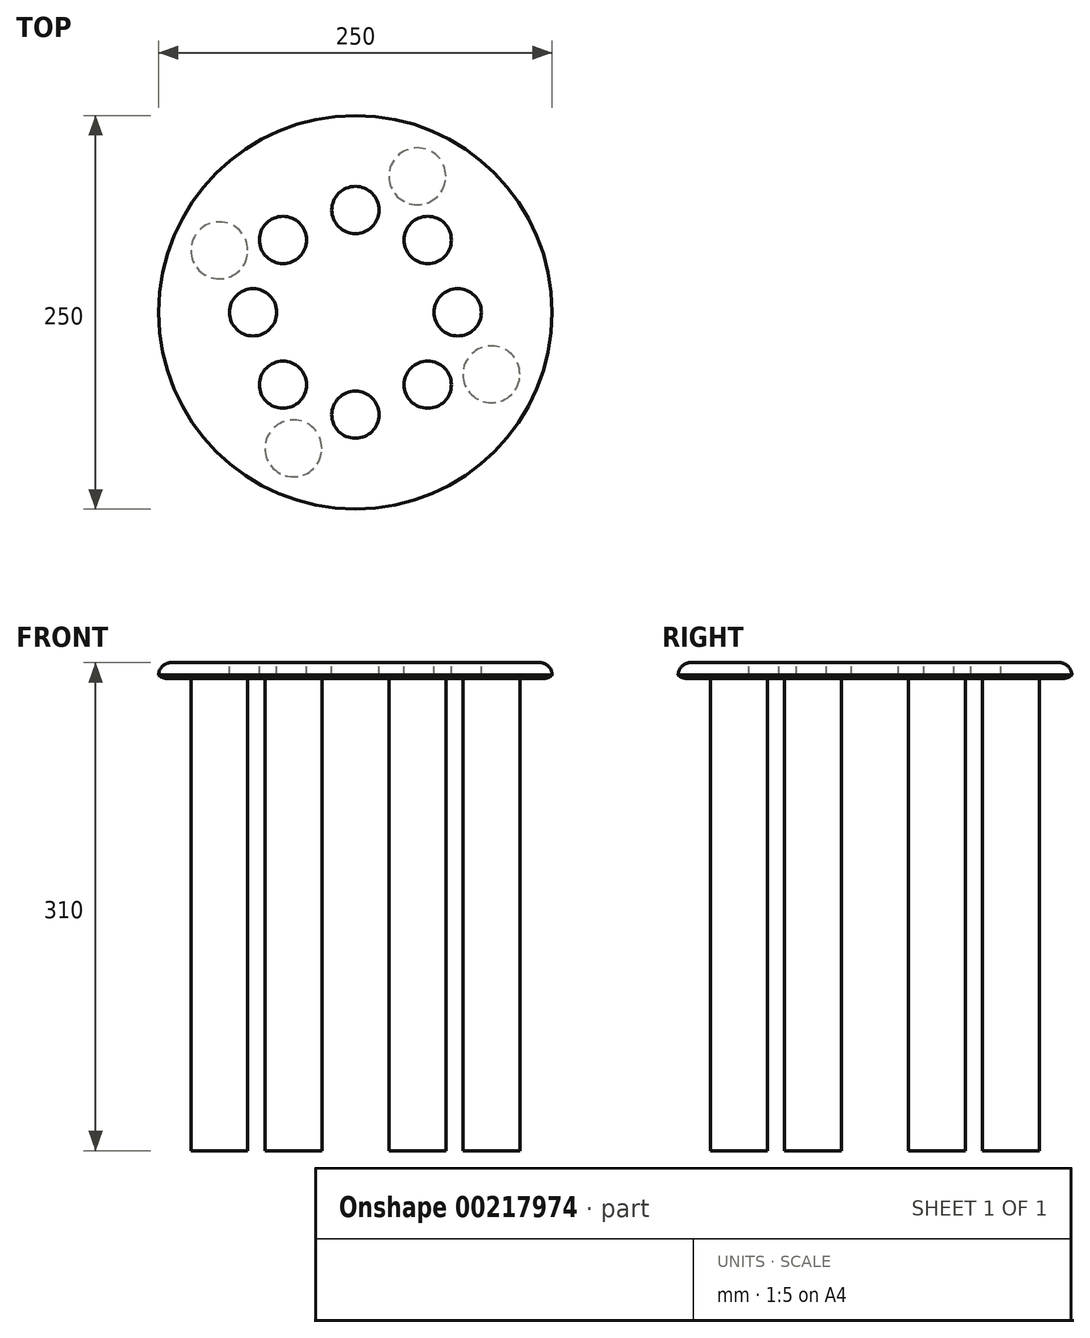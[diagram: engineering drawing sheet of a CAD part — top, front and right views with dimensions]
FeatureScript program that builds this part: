
annotation { "Feature Type Name" : "Feature", "Feature Type Description" : "" }
export const myFeature = defineFeature(function(context is Context, id is Id, definition is map)
    precondition{}
    {
        {
            var Q0;
            Q0=qCreatedBy(makeId("Top.planeOp"),FACE);
            var sketch = newSketch(context, id + "F0", { "sketchPlane" : qUnion([Q0])});
            skCircle(sketch, "E0", {"center": v(0, 0) * mm, "radius": 125 * mm});
            skSolve(sketch);
        }
        {
            var Q0;
            Q0=makeQuery(id+"F0.imprint","IMPRINT",FACE,{"disambiguationData":[TD([[makeQuery(id+"F0.imprint","IMPRINT",EDGE,{"derivedFrom":sQuery(id+"F0.wireOp",EDGE,"E0")}),1.0]])]});
            var sketch = newSketch(context, id + "F1", { "sketchPlane" : qUnion([Q0])});
            skCircle(sketch, "E1", {"center": v(0, 65) * mm, "radius": 15 * mm});
            skCircle(sketch, "E2.1.0", {"center": v(-45.96, 45.96) * mm, "radius": 15 * mm});
            skCircle(sketch, "E2.2.0", {"center": v(-65, 0) * mm, "radius": 15 * mm});
            skCircle(sketch, "E2.3.0", {"center": v(-45.96, -45.96) * mm, "radius": 15 * mm});
            skCircle(sketch, "E2.4.0", {"center": v(0, -65) * mm, "radius": 15 * mm});
            skCircle(sketch, "E2.5.0", {"center": v(45.96, -45.96) * mm, "radius": 15 * mm});
            skCircle(sketch, "E2.6.0", {"center": v(65, 0) * mm, "radius": 15 * mm});
            skCircle(sketch, "E2.7.0", {"center": v(45.96, 45.96) * mm, "radius": 15 * mm});
            skPoint(sketch, "E2.center", {"position": v(0, 0) * mm});
            skSolve(sketch);
        }
        {
            var Q0;
            Q0=makeQuery(id+"F0.imprint","IMPRINT",FACE,{"disambiguationData":[TD([[makeQuery(id+"F0.imprint","IMPRINT",EDGE,{"derivedFrom":sQuery(id+"F0.wireOp",EDGE,"E0")}),1.0]])]});
            extrude(context, id + "F2", {"entities" : qUnion([Q0]), "depth" : 10 * mm});
        }
        {
            var Q0;
            Q0=makeQuery(id+"F1.imprint","IMPRINT",FACE,{"disambiguationData":[TD([[makeQuery(id+"F1.imprint","IMPRINT",EDGE,{"derivedFrom":sQuery(id+"F1.wireOp",EDGE,"E2.3.0")}),1.0]])]});
            var Q1;
            Q1=makeQuery(id+"F1.imprint","IMPRINT",FACE,{"disambiguationData":[TD([[makeQuery(id+"F1.imprint","IMPRINT",EDGE,{"derivedFrom":sQuery(id+"F1.wireOp",EDGE,"E2.2.0")}),1.0]])]});
            var Q2;
            Q2=makeQuery(id+"F1.imprint","IMPRINT",FACE,{"disambiguationData":[TD([[makeQuery(id+"F1.imprint","IMPRINT",EDGE,{"derivedFrom":sQuery(id+"F1.wireOp",EDGE,"E1")}),1.0]])]});
            var Q3;
            Q3=makeQuery(id+"F1.imprint","IMPRINT",FACE,{"disambiguationData":[TD([[makeQuery(id+"F1.imprint","IMPRINT",EDGE,{"derivedFrom":sQuery(id+"F1.wireOp",EDGE,"E2.4.0")}),1.0]])]});
            var Q4;
            Q4=makeQuery(id+"F1.imprint","IMPRINT",FACE,{"disambiguationData":[TD([[makeQuery(id+"F1.imprint","IMPRINT",EDGE,{"derivedFrom":sQuery(id+"F1.wireOp",EDGE,"E2.5.0")}),1.0]])]});
            var Q5;
            Q5=makeQuery(id+"F1.imprint","IMPRINT",FACE,{"disambiguationData":[TD([[makeQuery(id+"F1.imprint","IMPRINT",EDGE,{"derivedFrom":sQuery(id+"F1.wireOp",EDGE,"E2.6.0")}),1.0]])]});
            var Q6;
            Q6=makeQuery(id+"F1.imprint","IMPRINT",FACE,{"disambiguationData":[TD([[makeQuery(id+"F1.imprint","IMPRINT",EDGE,{"derivedFrom":sQuery(id+"F1.wireOp",EDGE,"E2.7.0")}),1.0]])]});
            var Q7;
            Q7=makeQuery(id+"F1.imprint","IMPRINT",FACE,{"disambiguationData":[TD([[makeQuery(id+"F1.imprint","IMPRINT",EDGE,{"derivedFrom":sQuery(id+"F1.wireOp",EDGE,"E2.1.0")}),1.0]])]});
            extrude(context, id + "F3", {"entities" : qUnion([Q0, Q1, Q2, Q3, Q4, Q5, Q6, Q7]), "operationType" : NewBodyOperationType.ADD, "depth" : 39 * mm});
        }
        {
            var Q0;
            Q0=makeQuery(id+"F3.opExtrude","CAP_FACE",FACE,{"disambiguationData":[OSD([sQuery(id+"F1.wireOp",EDGE,"E2.3.0")])],"isStart":false});
            var Q1;
            Q1=makeQuery(id+"F3.opExtrude","CAP_FACE",FACE,{"disambiguationData":[OSD([sQuery(id+"F1.wireOp",EDGE,"E2.4.0")])],"isStart":false});
            var Q2;
            Q2=makeQuery(id+"F3.opExtrude","CAP_FACE",FACE,{"disambiguationData":[OSD([sQuery(id+"F1.wireOp",EDGE,"E2.5.0")])],"isStart":false});
            var Q3;
            Q3=makeQuery(id+"F3.opExtrude","CAP_FACE",FACE,{"disambiguationData":[OSD([sQuery(id+"F1.wireOp",EDGE,"E2.6.0")])],"isStart":false});
            var Q4;
            Q4=makeQuery(id+"F3.opExtrude","CAP_FACE",FACE,{"disambiguationData":[OSD([sQuery(id+"F1.wireOp",EDGE,"E2.7.0")])],"isStart":false});
            var Q5;
            Q5=makeQuery(id+"F3.opExtrude","CAP_FACE",FACE,{"disambiguationData":[OSD([sQuery(id+"F1.wireOp",EDGE,"E1")])],"isStart":false});
            var Q6;
            Q6=makeQuery(id+"F3.opExtrude","CAP_FACE",FACE,{"disambiguationData":[OSD([sQuery(id+"F1.wireOp",EDGE,"E2.1.0")])],"isStart":false});
            var Q7;
            Q7=makeQuery(id+"F3.opExtrude","CAP_FACE",FACE,{"disambiguationData":[OSD([sQuery(id+"F1.wireOp",EDGE,"E2.2.0")])],"isStart":false});
            extrude(context, id + "F4", {"entities" : qUnion([Q0, Q1, Q2, Q3, Q4, Q5, Q6, Q7]), "operationType" : NewBodyOperationType.REMOVE, "oppositeDirection" : true, "depth" : 107 * mm});
        }
        {
            var Q0;
            Q0=makeQuery(id+"F2.opExtrude","CAP_EDGE",EDGE,{"disambiguationData":[OSD([sQuery(id+"F0.wireOp",EDGE,"E0")])],"isStart":false});
            fillet(context, id + "F5", {"entities" : qUnion([Q0]), "radius" : 8 * mm, "tangentPropagation" : true, "allowEdgeOverflow" : false});
        }
        {
            var Q0;
            Q0=makeQuery(id+"F2.opExtrude","CAP_EDGE",EDGE,{"disambiguationData":[OSD([sQuery(id+"F0.wireOp",EDGE,"E0")])],"isStart":true});
            fillet(context, id + "F6", {"entities" : qUnion([Q0]), "radius" : 8 * mm, "tangentPropagation" : true, "allowEdgeOverflow" : false});
        }
        {
            var Q0;
            Q0=makeQuery(id+"F2.opExtrude","CAP_FACE",FACE,{"disambiguationData":[OSD([sQuery(id+"F0.wireOp",EDGE,"E0")])],"isStart":true});
            var sketch = newSketch(context, id + "F7", { "sketchPlane" : qUnion([Q0])});
            skCircle(sketch, "E3", {"center": v(39.36, -86.4) * mm, "radius": 18.07 * mm});
            skCircle(sketch, "E4.1.0", {"center": v(86.4, 39.36) * mm, "radius": 18.07 * mm});
            skCircle(sketch, "E4.2.0", {"center": v(-39.36, 86.4) * mm, "radius": 18.07 * mm});
            skCircle(sketch, "E4.3.0", {"center": v(-86.4, -39.36) * mm, "radius": 18.07 * mm});
            skPoint(sketch, "E4.center", {"position": v(0, 0) * mm});
            skSolve(sketch);
        }
        {
            var Q0;
            Q0=makeQuery(id+"F7.imprint","IMPRINT",FACE,{"disambiguationData":[TD([[makeQuery(id+"F7.imprint","IMPRINT",EDGE,{"derivedFrom":sQuery(id+"F7.wireOp",EDGE,"E3")}),1.0]])]});
            var Q1;
            Q1=makeQuery(id+"F7.imprint","IMPRINT",FACE,{"disambiguationData":[TD([[makeQuery(id+"F7.imprint","IMPRINT",EDGE,{"derivedFrom":sQuery(id+"F7.wireOp",EDGE,"E4.3.0")}),1.0]])]});
            var Q2;
            Q2=makeQuery(id+"F7.imprint","IMPRINT",FACE,{"disambiguationData":[TD([[makeQuery(id+"F7.imprint","IMPRINT",EDGE,{"derivedFrom":sQuery(id+"F7.wireOp",EDGE,"E4.2.0")}),1.0]])]});
            var Q3;
            Q3=makeQuery(id+"F7.imprint","IMPRINT",FACE,{"disambiguationData":[TD([[makeQuery(id+"F7.imprint","IMPRINT",EDGE,{"derivedFrom":sQuery(id+"F7.wireOp",EDGE,"E4.1.0")}),1.0]])]});
            extrude(context, id + "F8", {"entities" : qUnion([Q0, Q1, Q2, Q3]), "operationType" : NewBodyOperationType.ADD, "depth" : 300 * mm});
        }
    });
